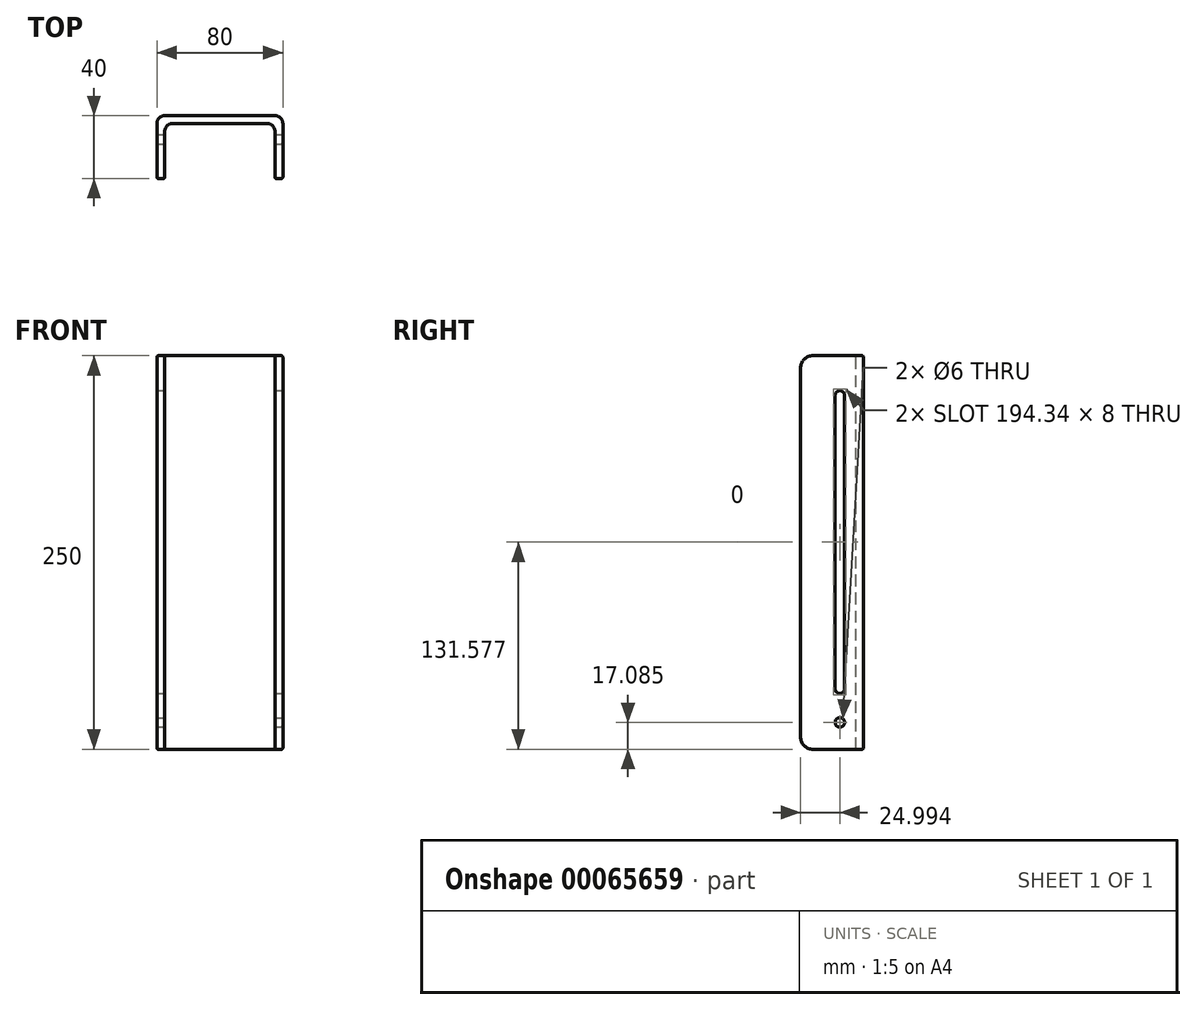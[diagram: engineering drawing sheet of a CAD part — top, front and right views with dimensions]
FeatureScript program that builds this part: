
annotation { "Feature Type Name" : "Feature", "Feature Type Description" : "" }
export const myFeature = defineFeature(function(context is Context, id is Id, definition is map)
    precondition{}
    {
        {
            var Q0;
            Q0=qCreatedBy(makeId("Top.planeOp"),FACE);
            var sketch = newSketch(context, id + "F0", { "sketchPlane" : qUnion([Q0])});
            skLineSegment(sketch, "E0.bottom", {"start": v(-35, 30) * mm, "end": v(35, 30) * mm});
            skLineSegment(sketch, "E0.top", {"start": v(-40, -10) * mm, "end": v(-35, -10) * mm});
            skLineSegment(sketch, "E0.left", {"start": v(-40, 25) * mm, "end": v(-40, -10) * mm});
            skLineSegment(sketch, "E0.right", {"start": v(40, 25) * mm, "end": v(40, -10) * mm});
            skLineSegment(sketch, "E1.0", {"start": v(-30, 25) * mm, "end": v(30, 25) * mm});
            skLineSegment(sketch, "E1.1", {"start": v(-35, 20) * mm, "end": v(-35, -10) * mm});
            skLineSegment(sketch, "E2.0", {"start": v(35, 20) * mm, "end": v(35, -10) * mm});
            skLineSegment(sketch, "E3.trimOffspring", {"start": v(35, -10) * mm, "end": v(40, -10) * mm});
            skPoint(sketch, "E4.visualSharp", {"position": v(-40, 30) * mm});
            skArc(sketch, "E4.filletArc", {"start": v(-35, 30) * mm, "mid": v(-38.54, 28.54) * mm, "end": v(-40, 25) * mm});
            skArc(sketch, "E5.filletArc", {"start": v(-30, 25) * mm, "mid": v(-33.54, 23.54) * mm, "end": v(-35, 20) * mm});
            skPoint(sketch, "E6.visualSharp", {"position": v(35, 25) * mm});
            skArc(sketch, "E6.filletArc", {"start": v(35, 20) * mm, "mid": v(33.54, 23.54) * mm, "end": v(30, 25) * mm});
            skPoint(sketch, "E7.visualSharp", {"position": v(40, 30) * mm});
            skArc(sketch, "E7.filletArc", {"start": v(40, 25) * mm, "mid": v(38.54, 28.54) * mm, "end": v(35, 30) * mm});
            skSolve(sketch);
        }
        {
            var Q0;
            Q0=makeQuery(id+"F0.imprint","IMPRINT",FACE,{"disambiguationData":[TD([[makeQuery(id+"F0.imprint","IMPRINT",EDGE,{"derivedFrom":sQuery(id+"F0.wireOp",EDGE,"E0.bottom")}),-1.0]])]});
            extrude(context, id + "F1", {"entities" : qUnion([Q0]), "depth" : 250 * mm});
        }
        {
            var Q0;
            Q0=qCreatedBy(makeId("Right.planeOp"),FACE);
            var sketch = newSketch(context, id + "F2", { "sketchPlane" : qUnion([Q0])});
            skCircle(sketch, "E8", {"center": v(15, 17.09) * mm, "radius": 3 * mm});
            skArc(sketch, "E9", {"start": v(18, 224.75) * mm, "mid": v(15, 227.75) * mm, "end": v(12, 224.75) * mm});
            skArc(sketch, "E10", {"start": v(12, 38.4) * mm, "mid": v(15, 35.4) * mm, "end": v(18, 38.4) * mm});
            skLineSegment(sketch, "E11.0", {"start": v(18, 192.73) * mm, "end": v(18, 224.75) * mm});
            skLineSegment(sketch, "E12.0", {"start": v(18, 38.4) * mm, "end": v(18, 192.73) * mm});
            skLineSegment(sketch, "E13.0", {"start": v(12, 192.73) * mm, "end": v(12, 224.75) * mm});
            skLineSegment(sketch, "E14.0", {"start": v(12, 38.4) * mm, "end": v(12, 192.73) * mm});
            skSolve(sketch);
        }
        {
            var Q0;
            Q0=makeQuery(id+"F2.imprint","IMPRINT",FACE,{"disambiguationData":[TD([[makeQuery(id+"F2.imprint","IMPRINT",EDGE,{"derivedFrom":sQuery(id+"F2.wireOp",EDGE,"E9")}),1.0]])]});
            var Q1;
            Q1=makeQuery(id+"F2.imprint","IMPRINT",FACE,{"disambiguationData":[TD([[makeQuery(id+"F2.imprint","IMPRINT",EDGE,{"derivedFrom":sQuery(id+"F2.wireOp",EDGE,"E8")}),1.0]])]});
            extrude(context, id + "F3", {"entities" : qUnion([Q0, Q1]), "operationType" : NewBodyOperationType.REMOVE, "endBound" : BoundingType.SYMMETRIC, "oppositeDirection" : true, "depth" : 100 * mm});
        }
        {
            var Q0;
            Q0=makeQuery(id+"F1.opExtrude","CAP_EDGE",EDGE,{"disambiguationData":[OSD([sQuery(id+"F0.wireOp",EDGE,"E0.top")])],"isStart":false});
            var Q1;
            Q1=makeQuery(id+"F1.opExtrude","CAP_EDGE",EDGE,{"disambiguationData":[OSD([sQuery(id+"F0.wireOp",EDGE,"E3.trimOffspring")])],"isStart":false});
            var Q2;
            Q2=makeQuery(id+"F1.opExtrude","CAP_EDGE",EDGE,{"disambiguationData":[OSD([sQuery(id+"F0.wireOp",EDGE,"E0.top")])],"isStart":true});
            var Q3;
            Q3=makeQuery(id+"F1.opExtrude","CAP_EDGE",EDGE,{"disambiguationData":[OSD([sQuery(id+"F0.wireOp",EDGE,"E3.trimOffspring")])],"isStart":true});
            fillet(context, id + "F4", {"entities" : qUnion([Q0, Q1, Q2, Q3]), "radius" : 8 * mm, "tangentPropagation" : true, "allowEdgeOverflow" : false});
        }
        {
            var Q0;
            Q0=makeQuery(id+"F1.opExtrude","CAP_EDGE",EDGE,{"disambiguationData":[OSD([sQuery(id+"F0.wireOp",EDGE,"E0.left")])],"isStart":false});
            var Q1;
            Q1=makeQuery(id+"F1.opExtrude","CAP_EDGE",EDGE,{"disambiguationData":[OSD([sQuery(id+"F0.wireOp",EDGE,"E1.1")])],"isStart":false});
            var Q2;
            Q2=makeQuery(id+"F3.boolean.opBoolean","INTERSECT",EDGE,{"derivedFrom":[makeQuery(id+"F1.opExtrude","SWEPT_FACE",FACE,{"disambiguationData":[OSD([sQuery(id+"F0.wireOp",EDGE,"E0.left")])]}),makeQuery(id+"F3.opExtrude","SWEPT_FACE",FACE,{"disambiguationData":[OSD([sQuery(id+"F2.wireOp",EDGE,"E11.0"),sQuery(id+"F2.wireOp",EDGE,"E12.0")])]})]});
            var Q3;
            Q3=makeQuery(id+"F3.boolean.opBoolean","INTERSECT",EDGE,{"derivedFrom":[makeQuery(id+"F1.opExtrude","SWEPT_FACE",FACE,{"disambiguationData":[OSD([sQuery(id+"F0.wireOp",EDGE,"E1.1")])]}),makeQuery(id+"F3.opExtrude","SWEPT_FACE",FACE,{"disambiguationData":[OSD([sQuery(id+"F2.wireOp",EDGE,"E11.0"),sQuery(id+"F2.wireOp",EDGE,"E12.0")])]})]});
            var Q4;
            Q4=makeQuery(id+"F3.boolean.opBoolean","INTERSECT",EDGE,{"derivedFrom":[makeQuery(id+"F1.opExtrude","SWEPT_FACE",FACE,{"disambiguationData":[OSD([sQuery(id+"F0.wireOp",EDGE,"E0.left")])]}),makeQuery(id+"F3.opExtrude","SWEPT_FACE",FACE,{"disambiguationData":[OSD([sQuery(id+"F2.wireOp",EDGE,"E8")])]})]});
            var Q5;
            Q5=makeQuery(id+"F3.boolean.opBoolean","INTERSECT",EDGE,{"derivedFrom":[makeQuery(id+"F1.opExtrude","SWEPT_FACE",FACE,{"disambiguationData":[OSD([sQuery(id+"F0.wireOp",EDGE,"E2.0")])]}),makeQuery(id+"F3.opExtrude","SWEPT_FACE",FACE,{"disambiguationData":[OSD([sQuery(id+"F2.wireOp",EDGE,"E8")])]})]});
            var Q6;
            Q6=makeQuery(id+"F3.boolean.opBoolean","INTERSECT",EDGE,{"derivedFrom":[makeQuery(id+"F1.opExtrude","SWEPT_FACE",FACE,{"disambiguationData":[OSD([sQuery(id+"F0.wireOp",EDGE,"E2.0")])]}),makeQuery(id+"F3.opExtrude","SWEPT_FACE",FACE,{"disambiguationData":[OSD([sQuery(id+"F2.wireOp",EDGE,"E11.0"),sQuery(id+"F2.wireOp",EDGE,"E12.0")])]})]});
            var Q7;
            Q7=makeQuery(id+"F3.boolean.opBoolean","INTERSECT",EDGE,{"derivedFrom":[makeQuery(id+"F1.opExtrude","SWEPT_FACE",FACE,{"disambiguationData":[OSD([sQuery(id+"F0.wireOp",EDGE,"E0.right")])]}),makeQuery(id+"F3.opExtrude","SWEPT_FACE",FACE,{"disambiguationData":[OSD([sQuery(id+"F2.wireOp",EDGE,"E11.0"),sQuery(id+"F2.wireOp",EDGE,"E12.0")])]})]});
            var Q8;
            Q8=makeQuery(id+"F3.boolean.opBoolean","INTERSECT",EDGE,{"derivedFrom":[makeQuery(id+"F1.opExtrude","SWEPT_FACE",FACE,{"disambiguationData":[OSD([sQuery(id+"F0.wireOp",EDGE,"E0.right")])]}),makeQuery(id+"F3.opExtrude","SWEPT_FACE",FACE,{"disambiguationData":[OSD([sQuery(id+"F2.wireOp",EDGE,"E8")])]})]});
            var Q9;
            Q9=makeQuery(id+"F3.boolean.opBoolean","INTERSECT",EDGE,{"derivedFrom":[makeQuery(id+"F1.opExtrude","SWEPT_FACE",FACE,{"disambiguationData":[OSD([sQuery(id+"F0.wireOp",EDGE,"E1.1")])]}),makeQuery(id+"F3.opExtrude","SWEPT_FACE",FACE,{"disambiguationData":[OSD([sQuery(id+"F2.wireOp",EDGE,"E8")])]})]});
            fillet(context, id + "F5", {"entities" : qUnion([Q0, Q1, Q2, Q3, Q4, Q5, Q6, Q7, Q8, Q9]), "radius" : 1 * mm, "tangentPropagation" : true, "allowEdgeOverflow" : false});
        }
    });
